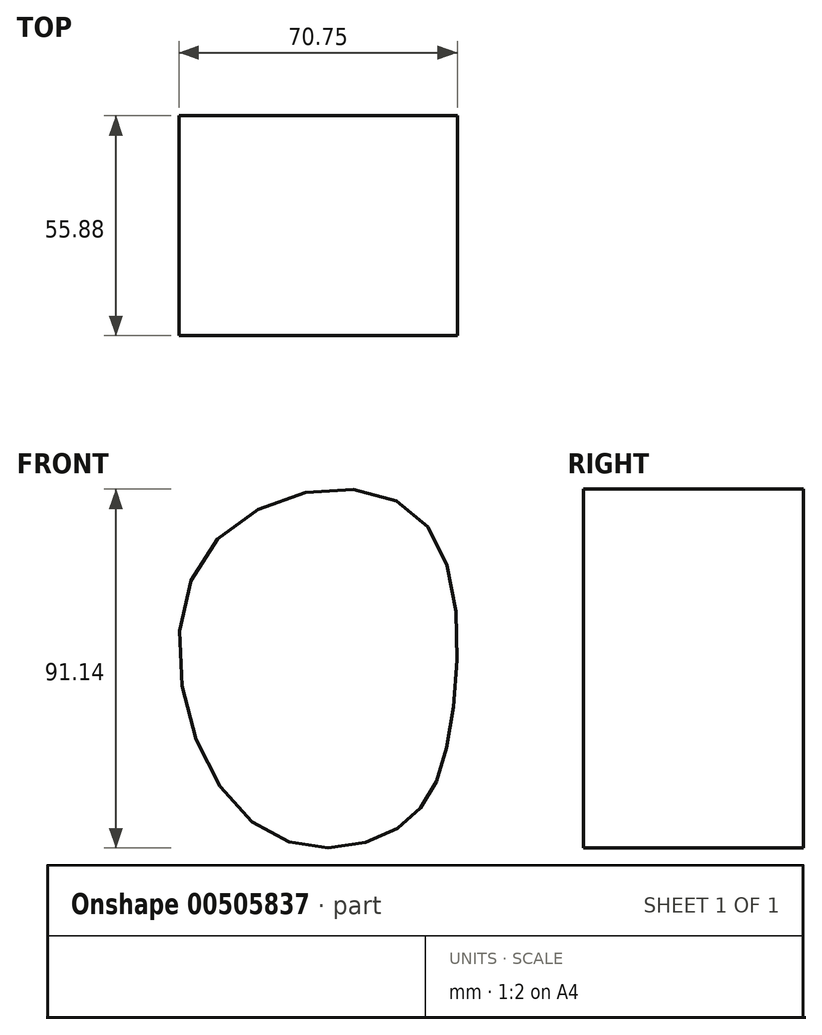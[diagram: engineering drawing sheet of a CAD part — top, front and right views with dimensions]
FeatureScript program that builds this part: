
annotation { "Feature Type Name" : "Feature", "Feature Type Description" : "" }
export const myFeature = defineFeature(function(context is Context, id is Id, definition is map)
    precondition{}
    {
        {
            var Q0;
            Q0=qCreatedBy(makeId("Front.planeOp"),FACE);
            var sketch = newSketch(context, id + "F0", { "sketchPlane" : qUnion([Q0])});
            skFitSpline(sketch, "E0", {"points": [v(-14.38, -37.3) * mm, v(22.92, -38.66) * mm, v(36.4, -11.01) * mm, v(25.62, 42.25) * mm, v(-27.2, 29.44) * mm, v(-14.38, -37.3) * mm]});
            skSolve(sketch);
        }
        {
            var Q0;
            Q0 = qSketchRegion(id + "F0", true);
            extrude(context, id + "F1", {"entities" : qUnion([Q0]), "depth" : 55.88 * mm});
        }
    });
